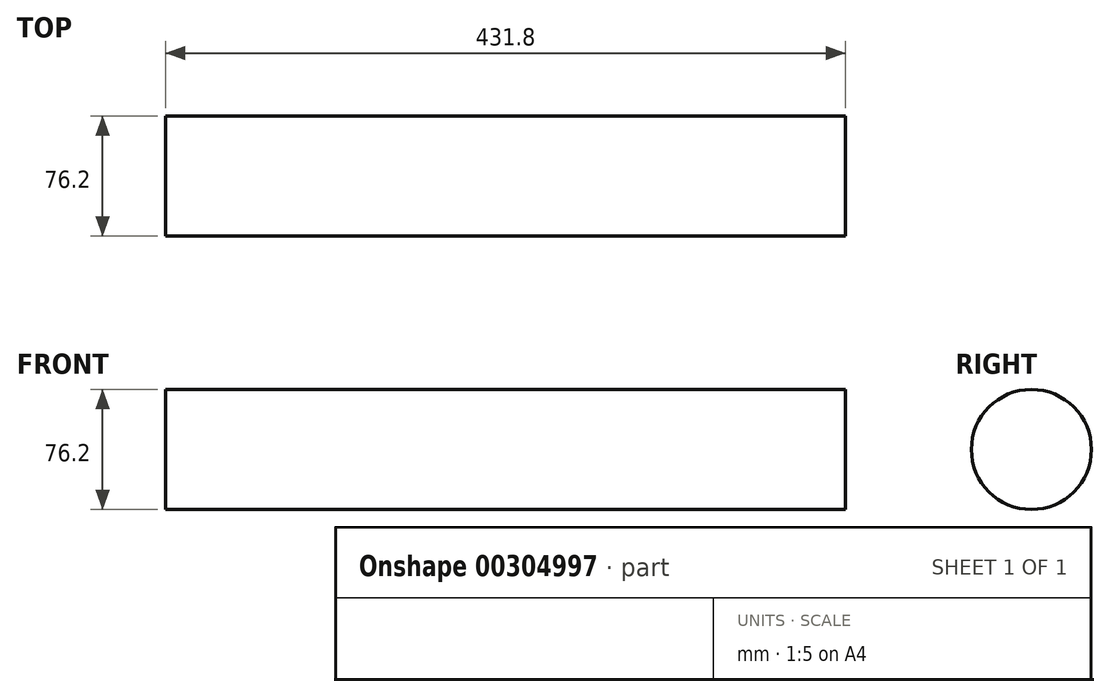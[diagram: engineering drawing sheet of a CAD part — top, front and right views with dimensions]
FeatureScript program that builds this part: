
annotation { "Feature Type Name" : "Feature", "Feature Type Description" : "" }
export const myFeature = defineFeature(function(context is Context, id is Id, definition is map)
    precondition{}
    {
        {
            var Q0;
            Q0=qCreatedBy(makeId("Right.planeOp"),FACE);
            var sketch = newSketch(context, id + "F0", { "sketchPlane" : qUnion([Q0])});
            skCircle(sketch, "E0", {"center": v(0, 0) * mm, "radius": 38.1 * mm});
            skSolve(sketch);
        }
        {
            var Q0;
            Q0=qCreatedBy(makeId("Front.planeOp"),FACE);
            var sketch = newSketch(context, id + "F1", { "sketchPlane" : qUnion([Q0])});
            skLineSegment(sketch, "E1", {"start": v(0, 38.1) * mm, "end": v(-60.05, 0) * mm});
            skLineSegment(sketch, "E2", {"start": v(-60.05, 0) * mm, "end": v(0, -38.1) * mm});
            skSolve(sketch);
        }
        {
            var Q0;
            Q0=makeQuery(id+"F0.imprint","IMPRINT",FACE,{"disambiguationData":[TD([[makeQuery(id+"F0.imprint","IMPRINT",EDGE,{"derivedFrom":sQuery(id+"F0.wireOp",EDGE,"E0")}),1.0]])]});
            extrude(context, id + "F2", {"entities" : qUnion([Q0]), "depth" : 431.8 * mm});
        }
        {
            var Q0;
            Q0=qCreatedBy(makeId("Front.planeOp"),FACE);
            var sketch = newSketch(context, id + "F3", { "sketchPlane" : qUnion([Q0])});
            skLineSegment(sketch, "E3", {"start": v(0, 0) * mm, "end": v(-59.76, 0) * mm});
            skSolve(sketch);
        }
        {
            var Q0;
            Q0=sQuery(id+"F1.wireOp",EDGE,"E1");
            var Q1;
            Q1=sQuery(id+"F3.wireOp",EDGE,"E3");
            revolve(context, id + "F4", {"bodyType" : ToolBodyType.SURFACE, "surfaceEntities" : qUnion([Q0]), "axis" : qUnion([Q1]), "revolveType" : RevolveType.FULL});
        }
    });
